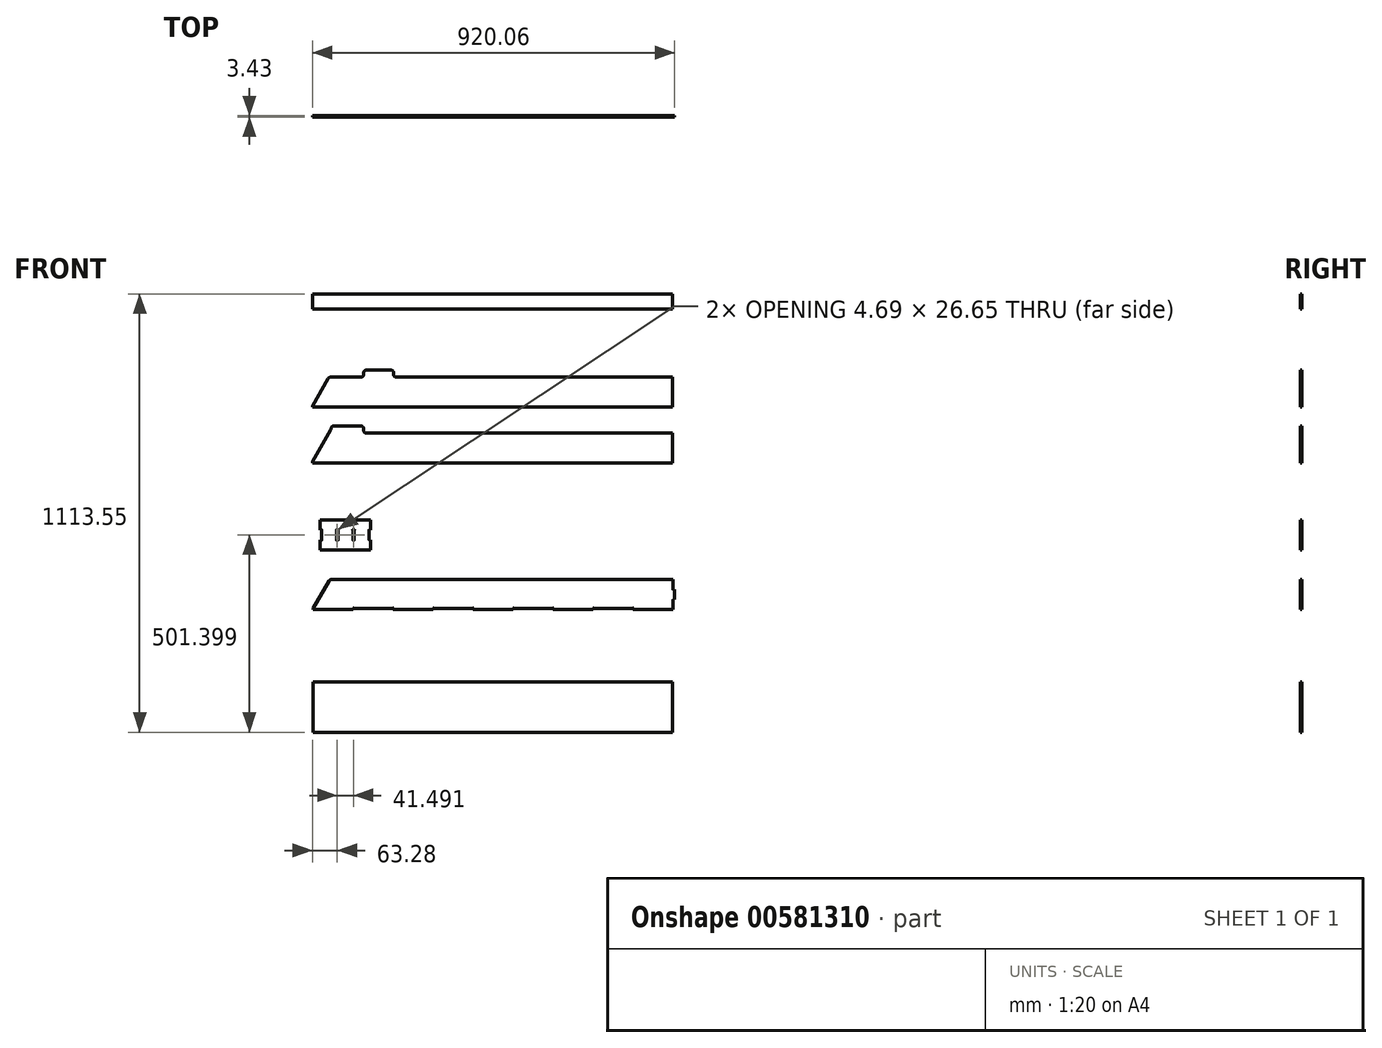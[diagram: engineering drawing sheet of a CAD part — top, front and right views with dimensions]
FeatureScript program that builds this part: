
annotation { "Feature Type Name" : "Feature", "Feature Type Description" : "" }
export const myFeature = defineFeature(function(context is Context, id is Id, definition is map)
    precondition{}
    {
        {
            var Q0;
            Q0=qCreatedBy(makeId("Front.planeOp"),FACE);
            var sketch = newSketch(context, id + "F0", { "sketchPlane" : qUnion([Q0])});
            skLineSegment(sketch, "E0", {"start": v(-436.83, -273.53) * mm, "end": v(477.57, -273.53) * mm, "construction": true});
            skLineSegment(sketch, "E1", {"start": v(20.37, -273.53) * mm, "end": v(20.37, -235.43) * mm, "construction": true});
            skLineSegment(sketch, "E2.trimOffspring", {"start": v(-333.7, -235.43) * mm, "end": v(-234.44, -235.43) * mm});
            skLineSegment(sketch, "E3", {"start": v(-436.83, -311.63) * mm, "end": v(-436.83, -273.53) * mm});
            skLineSegment(sketch, "E4", {"start": v(477.57, -235.43) * mm, "end": v(477.57, -260.24) * mm});
            skLineSegment(sketch, "E5", {"start": v(-438.12, -216.33) * mm, "end": v(-437.43, -216.38) * mm, "construction": true});
            skPoint(sketch, "E6.newPointA", {"position": v(-437.43, -216.33) * mm});
            skPoint(sketch, "E6.newPointB", {"position": v(-438.12, -235.43) * mm});
            skArc(sketch, "E7", {"start": v(23.28, -210.74) * mm, "mid": v(20.37, -210.03) * mm, "end": v(17.45, -210.74) * mm});
            skLineSegment(sketch, "E8", {"start": v(14.02, -216.38) * mm, "end": v(26.72, -216.38) * mm, "construction": true});
            skLineSegment(sketch, "E9", {"start": v(14.02, -216.33) * mm, "end": v(14.02, -216.38) * mm});
            skLineSegment(sketch, "E10.trimOffspring", {"start": v(72.7, -235.43) * mm, "end": v(171.96, -235.43) * mm});
            skPoint(sketch, "E11.visualSharp", {"position": v(14.02, -235.43) * mm});
            skPoint(sketch, "E12.visualSharp", {"position": v(34.05, -235.43) * mm});
            skArc(sketch, "E13.MirrorCS", {"start": v(24.77, -335.26) * mm, "mid": v(20.37, -337.03) * mm, "end": v(15.96, -335.26) * mm});
            skCircle(sketch, "E14.MirrorC", {"center": v(20.37, -330.68) * mm, "radius": 2.67 * mm});
            skLineSegment(sketch, "E15.trimOffspring", {"start": v(-436.83, -273.53) * mm, "end": v(-436.83, -239.3) * mm});
            skLineSegment(sketch, "E16.MirrorCS", {"start": v(480.98, -260.75) * mm, "end": v(480.98, -273.5) * mm});
            skLineSegment(sketch, "E17.MirrorCS", {"start": v(478.04, -286.15) * mm, "end": v(479.7, -286.15) * mm});
            skLineSegment(sketch, "E18", {"start": v(480.98, -260.75) * mm, "end": v(478.07, -260.75) * mm});
            skLineSegment(sketch, "E19.trimOffspring", {"start": v(477.57, -286.82) * mm, "end": v(477.57, -311.63) * mm});
            skArc(sketch, "E20", {"start": v(477.57, -260.24) * mm, "mid": v(477.2, -261.1) * mm, "end": v(478.07, -260.75) * mm});
            skArc(sketch, "E21.MirrorC", {"start": v(477.57, -286.82) * mm, "mid": v(477.15, -286.02) * mm, "end": v(478.04, -286.15) * mm});
            skLineSegment(sketch, "E22.MirrorCS", {"start": v(480.98, -286.32) * mm, "end": v(480.98, -273.57) * mm});
            skPoint(sketch, "E23.MirrorCS.start.orphan", {"position": v(477.57, -273.53) * mm});
            skPoint(sketch, "E12.filletArc.start.orphan", {"position": v(34.05, -229.12) * mm});
            skPoint(sketch, "E24.orphan", {"position": v(40.4, -235.43) * mm});
            skLineSegment(sketch, "E25", {"start": v(-335.23, -315.05) * mm, "end": v(-335.23, -312.14) * mm});
            skLineSegment(sketch, "E26", {"start": v(-334.73, -311.63) * mm, "end": v(-234.14, -311.63) * mm});
            skLineSegment(sketch, "E27", {"start": v(-233.63, -311.24) * mm, "end": v(-233.63, -312.14) * mm});
            skLineSegment(sketch, "E28", {"start": v(-132.03, -312.14) * mm, "end": v(-132.03, -311.24) * mm});
            skLineSegment(sketch, "E29", {"start": v(-131.53, -311.63) * mm, "end": v(-30.94, -311.63) * mm});
            skLineSegment(sketch, "E30", {"start": v(-30.43, -290.61) * mm, "end": v(-30.43, -312.14) * mm});
            skLineSegment(sketch, "E31", {"start": v(-182.83, -311.24) * mm, "end": v(-182.83, -379.42) * mm, "construction": true});
            skPoint(sketch, "E31.endSnap0", {"position": v(-182.83, -311.24) * mm});
            skCircle(sketch, "E32", {"center": v(-182.83, -330.53) * mm, "radius": 2.67 * mm});
            skArc(sketch, "E33", {"start": v(-185.77, -336.16) * mm, "mid": v(-184.34, -336.7) * mm, "end": v(-182.83, -336.88) * mm});
            skLineSegment(sketch, "E34", {"start": v(-233.63, -311.24) * mm, "end": v(-185.77, -336.16) * mm});
            skArc(sketch, "E35", {"start": v(-234.14, -311.63) * mm, "mid": v(-233.28, -311.27) * mm, "end": v(-233.63, -312.14) * mm});
            skArc(sketch, "E36.MirrorCS", {"start": v(-179.9, -336.16) * mm, "mid": v(-181.33, -336.7) * mm, "end": v(-182.83, -336.88) * mm});
            skLineSegment(sketch, "E37.MirrorCS", {"start": v(-132.03, -311.24) * mm, "end": v(-179.9, -336.16) * mm});
            skArc(sketch, "E38.MirrorCS", {"start": v(-131.53, -311.63) * mm, "mid": v(-132.4, -311.27) * mm, "end": v(-132.03, -312.14) * mm});
            skArc(sketch, "E39", {"start": v(-335.23, -312.14) * mm, "mid": v(-335.6, -311.27) * mm, "end": v(-334.73, -311.63) * mm});
            skLineSegment(sketch, "E40", {"start": v(-30.43, -290.61) * mm, "end": v(15.96, -335.26) * mm});
            skPoint(sketch, "E41.orphan", {"position": v(-403.8, -235.43) * mm});
            skLineSegment(sketch, "E42.MirrorCS", {"start": v(71.17, -290.61) * mm, "end": v(24.77, -335.26) * mm});
            skLineSegment(sketch, "E43.MirrorCS", {"start": v(71.17, -290.61) * mm, "end": v(71.17, -312.14) * mm});
            skLineSegment(sketch, "E44.MirrorCS", {"start": v(172.26, -311.63) * mm, "end": v(71.67, -311.63) * mm});
            skLineSegment(sketch, "E45.MirrorCS", {"start": v(172.77, -312.14) * mm, "end": v(172.77, -311.24) * mm});
            skArc(sketch, "E46.MirrorCS", {"start": v(172.26, -311.63) * mm, "mid": v(173.12, -311.27) * mm, "end": v(172.77, -312.14) * mm});
            skLineSegment(sketch, "E47.MirrorCS", {"start": v(172.77, -311.24) * mm, "end": v(220.63, -336.16) * mm});
            skArc(sketch, "E48.MirrorCS", {"start": v(220.63, -336.16) * mm, "mid": v(222.06, -336.7) * mm, "end": v(223.57, -336.88) * mm});
            skCircle(sketch, "E49.MirrorC", {"center": v(223.57, -330.53) * mm, "radius": 2.67 * mm});
            skArc(sketch, "E50.MirrorCS", {"start": v(226.5, -336.16) * mm, "mid": v(225.07, -336.7) * mm, "end": v(223.57, -336.88) * mm});
            skLineSegment(sketch, "E51.MirrorCS", {"start": v(274.37, -311.24) * mm, "end": v(226.5, -336.16) * mm});
            skLineSegment(sketch, "E52.MirrorCS", {"start": v(274.37, -311.24) * mm, "end": v(274.37, -312.14) * mm});
            skArc(sketch, "E53.MirrorCS", {"start": v(274.87, -311.63) * mm, "mid": v(274, -311.27) * mm, "end": v(274.37, -312.14) * mm});
            skLineSegment(sketch, "E54.MirrorCS", {"start": v(375.46, -311.63) * mm, "end": v(274.87, -311.63) * mm});
            skArc(sketch, "E55.MirrorCS", {"start": v(375.97, -312.14) * mm, "mid": v(376.32, -311.27) * mm, "end": v(375.46, -311.63) * mm});
            skLineSegment(sketch, "E56.MirrorCS", {"start": v(375.97, -315.05) * mm, "end": v(375.97, -312.14) * mm});
            skArc(sketch, "E57", {"start": v(71.17, -312.14) * mm, "mid": v(70.8, -311.27) * mm, "end": v(71.67, -311.63) * mm});
            skArc(sketch, "E58", {"start": v(-30.94, -311.63) * mm, "mid": v(-30.08, -311.27) * mm, "end": v(-30.43, -312.14) * mm});
            skCircle(sketch, "E59", {"center": v(-386.03, -216.38) * mm, "radius": 2.67 * mm});
            skArc(sketch, "E60", {"start": v(-388.95, -210.74) * mm, "mid": v(-386.03, -210.03) * mm, "end": v(-383.12, -210.74) * mm});
            skLineSegment(sketch, "E61", {"start": v(-433.4, -233.66) * mm, "end": v(-388.95, -210.74) * mm});
            skLineSegment(sketch, "E62", {"start": v(-386.03, -216.38) * mm, "end": v(-386.03, -233.2) * mm, "construction": true});
            skPoint(sketch, "E63.orphan", {"position": v(-392.38, -216.38) * mm});
            skPoint(sketch, "E64.visualSharp", {"position": v(-436.83, -235.43) * mm});
            skArc(sketch, "E64.filletArc", {"start": v(-433.4, -233.66) * mm, "mid": v(-435.9, -236) * mm, "end": v(-436.83, -239.3) * mm});
            skLineSegment(sketch, "E65.MirrorCS", {"start": v(-336.6, -234.72) * mm, "end": v(-383.12, -210.74) * mm});
            skPoint(sketch, "E66.orphan", {"position": v(-379.68, -216.38) * mm});
            skArc(sketch, "E67.filletArc", {"start": v(-336.6, -234.72) * mm, "mid": v(-335.2, -235.25) * mm, "end": v(-333.7, -235.43) * mm});
            skLineSegment(sketch, "E68.MirrorCS", {"start": v(-436.83, -311.63) * mm, "end": v(-388.95, -336.32) * mm});
            skArc(sketch, "E69.MirrorCS", {"start": v(-388.95, -336.32) * mm, "mid": v(-386.03, -337.03) * mm, "end": v(-383.12, -336.32) * mm});
            skCircle(sketch, "E70.MirrorC", {"center": v(-386.03, -330.68) * mm, "radius": 2.67 * mm});
            skLineSegment(sketch, "E71.MirrorCS", {"start": v(-335.23, -311.63) * mm, "end": v(-383.12, -336.32) * mm});
            skPoint(sketch, "E72.orphan", {"position": v(-436.83, -311.63) * mm});
            skLineSegment(sketch, "E73.MirrorCS", {"start": v(69.8, -234.72) * mm, "end": v(23.28, -210.74) * mm});
            skCircle(sketch, "E74.MirrorC", {"center": v(20.37, -216.38) * mm, "radius": 2.67 * mm});
            skLineSegment(sketch, "E75.MirrorCS", {"start": v(-29.07, -234.72) * mm, "end": v(17.45, -210.74) * mm});
            skArc(sketch, "E76.MirrorCS", {"start": v(-29.07, -234.72) * mm, "mid": v(-30.48, -235.25) * mm, "end": v(-31.98, -235.43) * mm});
            skPoint(sketch, "E77.orphan", {"position": v(-3.75, -235.43) * mm});
            skPoint(sketch, "E78.orphan", {"position": v(44.48, -235.43) * mm});
            skPoint(sketch, "E79.visualSharp", {"position": v(71.17, -235.43) * mm});
            skArc(sketch, "E79.filletArc", {"start": v(69.8, -234.72) * mm, "mid": v(71.2, -235.25) * mm, "end": v(72.7, -235.43) * mm});
            skLineSegment(sketch, "E80.MirrorCS", {"start": v(375.97, -311.63) * mm, "end": v(423.85, -336.32) * mm});
            skArc(sketch, "E81.MirrorCS", {"start": v(429.68, -336.32) * mm, "mid": v(426.77, -337.03) * mm, "end": v(423.85, -336.32) * mm});
            skLineSegment(sketch, "E82.MirrorCS", {"start": v(477.57, -311.63) * mm, "end": v(429.68, -336.32) * mm});
            skCircle(sketch, "E83.MirrorC", {"center": v(426.77, -330.68) * mm, "radius": 2.67 * mm});
            skLineSegment(sketch, "E84.MirrorCS", {"start": v(477.57, -235.43) * mm, "end": v(429.68, -210.74) * mm});
            skArc(sketch, "E85.MirrorCS", {"start": v(429.68, -210.74) * mm, "mid": v(426.77, -210.03) * mm, "end": v(423.85, -210.74) * mm});
            skCircle(sketch, "E86.MirrorC", {"center": v(426.77, -216.38) * mm, "radius": 2.67 * mm});
            skLineSegment(sketch, "E87.MirrorCS", {"start": v(377.33, -234.72) * mm, "end": v(423.85, -210.74) * mm});
            skPoint(sketch, "E88.orphan", {"position": v(444.53, -235.43) * mm});
            skPoint(sketch, "E89.visualSharp", {"position": v(375.97, -235.43) * mm});
            skArc(sketch, "E89.filletArc", {"start": v(374.42, -235.43) * mm, "mid": v(375.92, -235.25) * mm, "end": v(377.33, -234.72) * mm});
            skLineSegment(sketch, "E90.MirrorCS", {"start": v(-231.5, -234.71) * mm, "end": v(-185.77, -210.9) * mm});
            skLineSegment(sketch, "E91.MirrorCS", {"start": v(-134.16, -234.71) * mm, "end": v(-179.9, -210.9) * mm});
            skArc(sketch, "E92.MirrorCS", {"start": v(-185.77, -210.9) * mm, "mid": v(-184.34, -210.36) * mm, "end": v(-182.83, -210.18) * mm});
            skArc(sketch, "E93.MirrorCS", {"start": v(-179.9, -210.9) * mm, "mid": v(-181.33, -210.36) * mm, "end": v(-182.83, -210.18) * mm});
            skCircle(sketch, "E94.MirrorC", {"center": v(-182.83, -216.53) * mm, "radius": 2.67 * mm});
            skLineSegment(sketch, "E95.MirrorCS", {"start": v(174.9, -234.71) * mm, "end": v(220.63, -210.9) * mm});
            skArc(sketch, "E96.MirrorCS", {"start": v(220.63, -210.9) * mm, "mid": v(222.06, -210.36) * mm, "end": v(223.57, -210.18) * mm});
            skArc(sketch, "E97.MirrorCS", {"start": v(226.5, -210.9) * mm, "mid": v(225.07, -210.36) * mm, "end": v(223.57, -210.18) * mm});
            skLineSegment(sketch, "E98.MirrorCS", {"start": v(272.24, -234.71) * mm, "end": v(226.5, -210.9) * mm});
            skCircle(sketch, "E99.MirrorC", {"center": v(223.57, -216.53) * mm, "radius": 2.67 * mm});
            skLineSegment(sketch, "E100.trimOffspring", {"start": v(-131.23, -235.43) * mm, "end": v(-31.98, -235.43) * mm});
            skPoint(sketch, "E101.newPointA", {"position": v(-233.63, -235.82) * mm});
            skArc(sketch, "E101.filletArc", {"start": v(-234.44, -235.43) * mm, "mid": v(-232.93, -235.25) * mm, "end": v(-231.5, -234.71) * mm});
            skPoint(sketch, "E102.newPointA", {"position": v(-132.03, -235.82) * mm});
            skArc(sketch, "E102.filletArc", {"start": v(-134.16, -234.71) * mm, "mid": v(-132.74, -235.25) * mm, "end": v(-131.23, -235.43) * mm});
            skLineSegment(sketch, "E103.trimOffspring", {"start": v(275.17, -235.43) * mm, "end": v(374.42, -235.43) * mm});
            skPoint(sketch, "E104.newPointA", {"position": v(172.77, -235.82) * mm});
            skArc(sketch, "E104.filletArc", {"start": v(171.96, -235.43) * mm, "mid": v(173.47, -235.25) * mm, "end": v(174.9, -234.71) * mm});
            skPoint(sketch, "E105.newPointA", {"position": v(274.37, -235.82) * mm});
            skArc(sketch, "E105.filletArc", {"start": v(272.24, -234.71) * mm, "mid": v(273.66, -235.25) * mm, "end": v(275.17, -235.43) * mm});
            skSolve(sketch);
        }
        {
            var Q0;
            Q0=qCreatedBy(makeId("Front.planeOp"),FACE);
            var sketch = newSketch(context, id + "F1", { "sketchPlane" : qUnion([Q0])});
            skLineSegment(sketch, "E106.0", {"start": v(-444.44, -324.66) * mm, "end": v(-444.44, -235.76) * mm});
            skLineSegment(sketch, "E107.0", {"start": v(469.96, -235.76) * mm, "end": v(469.96, -324.66) * mm});
            skLineSegment(sketch, "E108.bottom", {"start": v(-444.44, -143.46) * mm, "end": v(469.96, -143.46) * mm});
            skLineSegment(sketch, "E108.top", {"start": v(-444.44, -181.56) * mm, "end": v(469.96, -181.56) * mm});
            skLineSegment(sketch, "E108.left", {"start": v(-444.44, -143.46) * mm, "end": v(-444.44, -181.56) * mm});
            skLineSegment(sketch, "E108.right", {"start": v(469.96, -143.46) * mm, "end": v(469.96, -181.56) * mm});
            skSolve(sketch);
        }
        {
            var Q0;
            Q0=makeQuery(id+"F1.imprint","IMPRINT",FACE,{"disambiguationData":[TD([[makeQuery(id+"F1.imprint","IMPRINT",EDGE,{"derivedFrom":sQuery(id+"F1.wireOp",EDGE,"E108.bottom")}),-1.0]])]});
            extrude(context, id + "F2", {"entities" : qUnion([Q0]), "depth" : 3.42 * mm, "offsetDistance" : 25.4 * mm});
        }
        {
            var Q0;
            Q0=qCreatedBy(makeId("Front.planeOp"),FACE);
            var sketch = newSketch(context, id + "F3", { "sketchPlane" : qUnion([Q0])});
            skLineSegment(sketch, "E109.0", {"start": v(-444.44, -324.66) * mm, "end": v(-444.44, -235.76) * mm});
            skLineSegment(sketch, "E110.0", {"start": v(469.96, -235.76) * mm, "end": v(469.96, -324.66) * mm});
            skLineSegment(sketch, "E111.bottom", {"start": v(-398.75, -354.83) * mm, "end": v(-320.6, -354.83) * mm});
            skLineSegment(sketch, "E111.top", {"start": v(-444.44, -431.03) * mm, "end": v(469.96, -431.03) * mm});
            skLineSegment(sketch, "E111.right", {"start": v(469.96, -354.83) * mm, "end": v(469.96, -431.03) * mm});
            skLineSegment(sketch, "E112.top", {"start": v(-307.9, -337.05) * mm, "end": v(-244.4, -337.05) * mm});
            skLineSegment(sketch, "E112.left", {"start": v(-314.24, -348.48) * mm, "end": v(-314.24, -343.4) * mm});
            skLineSegment(sketch, "E112.right", {"start": v(-238.04, -348.48) * mm, "end": v(-238.04, -343.4) * mm});
            skLineSegment(sketch, "E113.trimOffspring", {"start": v(-231.7, -354.83) * mm, "end": v(469.96, -354.83) * mm});
            skPoint(sketch, "E114.visualSharp", {"position": v(-314.24, -337.05) * mm});
            skArc(sketch, "E114.filletArc", {"start": v(-307.9, -337.05) * mm, "mid": v(-312.38, -338.9) * mm, "end": v(-314.24, -343.4) * mm});
            skPoint(sketch, "E115.visualSharp", {"position": v(-238.04, -337.05) * mm});
            skArc(sketch, "E115.filletArc", {"start": v(-238.04, -343.4) * mm, "mid": v(-239.9, -338.9) * mm, "end": v(-244.4, -337.05) * mm});
            skPoint(sketch, "E116.visualSharp", {"position": v(-314.24, -354.83) * mm});
            skArc(sketch, "E116.filletArc", {"start": v(-320.6, -354.83) * mm, "mid": v(-316.1, -352.97) * mm, "end": v(-314.24, -348.48) * mm});
            skPoint(sketch, "E117.visualSharp", {"position": v(-238.04, -354.83) * mm});
            skArc(sketch, "E117.filletArc", {"start": v(-238.04, -348.48) * mm, "mid": v(-236.18, -352.97) * mm, "end": v(-231.7, -354.83) * mm});
            skLineSegment(sketch, "E118", {"start": v(-444.44, -427.61) * mm, "end": v(-404.25, -358) * mm});
            skPoint(sketch, "E119.visualSharp", {"position": v(-402.42, -354.83) * mm});
            skArc(sketch, "E119.filletArc", {"start": v(-398.75, -354.83) * mm, "mid": v(-401.93, -355.68) * mm, "end": v(-404.25, -358) * mm});
            skLineSegment(sketch, "E120", {"start": v(-444.44, -324.66) * mm, "end": v(-444.44, -471.8) * mm, "construction": true});
            skLineSegment(sketch, "E121", {"start": v(469.96, -324.66) * mm, "end": v(469.96, -480.39) * mm, "construction": true});
            skPoint(sketch, "E122.0", {"position": v(-355.54, -235.76) * mm});
            skLineSegment(sketch, "E123", {"start": v(-444.44, -427.61) * mm, "end": v(-444.44, -431.03) * mm});
            skSolve(sketch);
        }
        {
            var Q0;
            Q0=makeQuery(id+"F3.imprint","IMPRINT",FACE,{"disambiguationData":[TD([[makeQuery(id+"F3.imprint","IMPRINT",EDGE,{"derivedFrom":sQuery(id+"F3.wireOp",EDGE,"E111.bottom")}),-1.0]])]});
            extrude(context, id + "F4", {"entities" : qUnion([Q0]), "depth" : 3.42 * mm, "offsetDistance" : 25.4 * mm});
        }
        {
            var Q0;
            Q0=qCreatedBy(makeId("Front.planeOp"),FACE);
            var sketch = newSketch(context, id + "F5", { "sketchPlane" : qUnion([Q0])});
            skPoint(sketch, "E124.0", {"position": v(-444.44, -431.03) * mm});
            skLineSegment(sketch, "E125.0", {"start": v(469.96, -354.83) * mm, "end": v(469.96, -431.03) * mm});
            skLineSegment(sketch, "E126", {"start": v(-444.44, -431.03) * mm, "end": v(-444.44, -515.14) * mm, "construction": true});
            skLineSegment(sketch, "E127", {"start": v(469.96, -431.03) * mm, "end": v(469.96, -621.54) * mm, "construction": true});
            skLineSegment(sketch, "E128", {"start": v(469.96, -496.68) * mm, "end": v(469.96, -572.88) * mm});
            skLineSegment(sketch, "E129", {"start": v(469.96, -572.88) * mm, "end": v(-444.44, -572.88) * mm});
            skPoint(sketch, "E130.0", {"position": v(-238.04, -348.48) * mm});
            skLineSegment(sketch, "E131.bottom", {"start": v(-390.43, -478.9) * mm, "end": v(-320.58, -478.9) * mm});
            skLineSegment(sketch, "E131.left", {"start": v(-396.78, -485.21) * mm, "end": v(-396.78, -485.25) * mm});
            skLineSegment(sketch, "E131.right", {"start": v(-314.23, -485.25) * mm, "end": v(-314.23, -490.33) * mm});
            skLineSegment(sketch, "E132.trimOffspring", {"start": v(-307.88, -496.68) * mm, "end": v(469.96, -496.68) * mm});
            skPoint(sketch, "E133.visualSharp", {"position": v(-396.78, -478.9) * mm});
            skArc(sketch, "E133.filletArc", {"start": v(-390.43, -478.9) * mm, "mid": v(-394.92, -480.76) * mm, "end": v(-396.78, -485.25) * mm});
            skPoint(sketch, "E134.visualSharp", {"position": v(-314.23, -478.9) * mm});
            skArc(sketch, "E134.filletArc", {"start": v(-314.23, -485.25) * mm, "mid": v(-316.1, -480.76) * mm, "end": v(-320.58, -478.9) * mm});
            skPoint(sketch, "E135.visualSharp", {"position": v(-314.23, -496.68) * mm});
            skArc(sketch, "E135.filletArc", {"start": v(-314.23, -490.33) * mm, "mid": v(-312.37, -494.82) * mm, "end": v(-307.88, -496.68) * mm});
            skPoint(sketch, "E136.visualSharp", {"position": v(-396.78, -515.14) * mm});
            skLineSegment(sketch, "E137", {"start": v(-444.44, -569.47) * mm, "end": v(-397.63, -488.39) * mm});
            skLineSegment(sketch, "E138.trimOffspring", {"start": v(-444.44, -569.47) * mm, "end": v(-444.44, -621.54) * mm, "construction": true});
            skLineSegment(sketch, "E139", {"start": v(-307.88, -496.68) * mm, "end": v(-396.78, -496.68) * mm, "construction": true});
            skArc(sketch, "E140.filletArc", {"start": v(-397.63, -488.39) * mm, "mid": v(-397, -486.86) * mm, "end": v(-396.78, -485.21) * mm});
            skLineSegment(sketch, "E141", {"start": v(-444.44, -572.88) * mm, "end": v(-444.44, -569.47) * mm});
            skSolve(sketch);
        }
        {
            var Q0;
            Q0=makeQuery(id+"F5.imprint","IMPRINT",FACE,{"disambiguationData":[TD([[makeQuery(id+"F5.imprint","IMPRINT",EDGE,{"derivedFrom":sQuery(id+"F5.wireOp",EDGE,"E128")}),-1.0]])]});
            extrude(context, id + "F6", {"entities" : qUnion([Q0]), "depth" : 3.4 * mm, "offsetDistance" : 25.4 * mm});
        }
        {
            var Q0;
            Q0=qCreatedBy(makeId("Front.planeOp"),FACE);
            var sketch = newSketch(context, id + "F7", { "sketchPlane" : qUnion([Q0])});
            skLineSegment(sketch, "E142.bottom", {"start": v(-424.4, -717.51) * mm, "end": v(-296.43, -717.51) * mm});
            skLineSegment(sketch, "E142.top", {"start": v(-424.4, -793.71) * mm, "end": v(-296.43, -793.71) * mm});
            skLineSegment(sketch, "E142.left", {"start": v(-424.4, -717.51) * mm, "end": v(-424.4, -742.78) * mm});
            skLineSegment(sketch, "E142.right", {"start": v(-296.43, -717.51) * mm, "end": v(-296.43, -742.78) * mm});
            skLineSegment(sketch, "E143", {"start": v(-424.4, -755.61) * mm, "end": v(-296.43, -755.61) * mm, "construction": true});
            skLineSegment(sketch, "E144", {"start": v(-360.41, -717.51) * mm, "end": v(-360.41, -793.71) * mm, "construction": true});
            skLineSegment(sketch, "E145", {"start": v(-424.4, -742.78) * mm, "end": v(-421.49, -742.78) * mm});
            skLineSegment(sketch, "E146", {"start": v(-420.98, -743.3) * mm, "end": v(-420.98, -755.61) * mm});
            skLineSegment(sketch, "E147.MirrorCS", {"start": v(-420.98, -767.93) * mm, "end": v(-420.98, -755.61) * mm});
            skLineSegment(sketch, "E148.MirrorCS", {"start": v(-424.4, -768.44) * mm, "end": v(-421.49, -768.44) * mm});
            skLineSegment(sketch, "E149.MirrorCS", {"start": v(-299.85, -743.3) * mm, "end": v(-299.85, -755.61) * mm});
            skLineSegment(sketch, "E150.MirrorCS", {"start": v(-296.43, -742.78) * mm, "end": v(-299.34, -742.78) * mm});
            skLineSegment(sketch, "E151.MirrorCS", {"start": v(-299.85, -767.93) * mm, "end": v(-299.85, -755.61) * mm});
            skLineSegment(sketch, "E152.MirrorCS", {"start": v(-296.43, -768.44) * mm, "end": v(-299.34, -768.44) * mm});
            skLineSegment(sketch, "E153.trimOffspring", {"start": v(-424.4, -768.44) * mm, "end": v(-424.4, -793.71) * mm});
            skLineSegment(sketch, "E154.trimOffspring", {"start": v(-296.43, -768.44) * mm, "end": v(-296.43, -793.71) * mm});
            skArc(sketch, "E155", {"start": v(-420.98, -743.3) * mm, "mid": v(-420.62, -742.42) * mm, "end": v(-421.49, -742.78) * mm});
            skArc(sketch, "E156.MirrorCS", {"start": v(-420.98, -767.93) * mm, "mid": v(-420.62, -768.8) * mm, "end": v(-421.49, -768.44) * mm});
            skArc(sketch, "E157.MirrorCS", {"start": v(-299.85, -743.3) * mm, "mid": v(-300.2, -742.42) * mm, "end": v(-299.34, -742.78) * mm});
            skArc(sketch, "E158.MirrorCS", {"start": v(-299.85, -767.93) * mm, "mid": v(-300.2, -768.8) * mm, "end": v(-299.34, -768.44) * mm});
            skLineSegment(sketch, "E159", {"start": v(-421.49, -742.78) * mm, "end": v(-383, -742.78) * mm, "construction": true});
            skLineSegment(sketch, "E160.MirrorCS", {"start": v(-421.49, -768.44) * mm, "end": v(-383, -768.44) * mm, "construction": true});
            skLineSegment(sketch, "E161", {"start": v(-383, -743.3) * mm, "end": v(-383, -755.61) * mm});
            skLineSegment(sketch, "E162", {"start": v(-379.31, -743.3) * mm, "end": v(-379.31, -755.61) * mm});
            skLineSegment(sketch, "E163", {"start": v(-382.5, -742.78) * mm, "end": v(-379.82, -742.78) * mm});
            skArc(sketch, "E164", {"start": v(-382.5, -742.78) * mm, "mid": v(-383.37, -742.42) * mm, "end": v(-383, -743.3) * mm});
            skArc(sketch, "E165", {"start": v(-379.31, -743.3) * mm, "mid": v(-378.95, -742.42) * mm, "end": v(-379.82, -742.78) * mm});
            skLineSegment(sketch, "E166.trimOffspring", {"start": v(-382.5, -742.78) * mm, "end": v(-338.33, -742.78) * mm, "construction": true});
            skLineSegment(sketch, "E167.MirrorCS", {"start": v(-379.31, -767.93) * mm, "end": v(-379.31, -755.61) * mm});
            skLineSegment(sketch, "E168.MirrorCS", {"start": v(-383, -767.93) * mm, "end": v(-383, -755.61) * mm});
            skArc(sketch, "E169.MirrorCS", {"start": v(-382.5, -768.44) * mm, "mid": v(-383.37, -768.8) * mm, "end": v(-383, -767.93) * mm});
            skArc(sketch, "E170.MirrorCS", {"start": v(-379.31, -767.93) * mm, "mid": v(-378.95, -768.8) * mm, "end": v(-379.82, -768.44) * mm});
            skLineSegment(sketch, "E171.MirrorCS", {"start": v(-383, -768.44) * mm, "end": v(-379.82, -768.44) * mm});
            skLineSegment(sketch, "E172.MirrorCS", {"start": v(-341.52, -743.3) * mm, "end": v(-341.52, -755.61) * mm});
            skArc(sketch, "E173.MirrorCS", {"start": v(-341.52, -743.3) * mm, "mid": v(-341.88, -742.42) * mm, "end": v(-341, -742.78) * mm});
            skLineSegment(sketch, "E174.MirrorCS", {"start": v(-338.33, -742.78) * mm, "end": v(-341, -742.78) * mm});
            skArc(sketch, "E175.MirrorCS", {"start": v(-338.33, -742.78) * mm, "mid": v(-337.46, -742.42) * mm, "end": v(-337.82, -743.3) * mm});
            skLineSegment(sketch, "E176.MirrorCS", {"start": v(-337.82, -743.3) * mm, "end": v(-337.82, -755.61) * mm});
            skLineSegment(sketch, "E177.MirrorCS", {"start": v(-337.82, -767.93) * mm, "end": v(-337.82, -755.61) * mm});
            skLineSegment(sketch, "E178.MirrorCS", {"start": v(-341.52, -767.93) * mm, "end": v(-341.52, -755.61) * mm});
            skArc(sketch, "E179.MirrorCS", {"start": v(-341.52, -767.93) * mm, "mid": v(-341.88, -768.8) * mm, "end": v(-341, -768.44) * mm});
            skArc(sketch, "E180.MirrorCS", {"start": v(-338.33, -768.44) * mm, "mid": v(-337.46, -768.8) * mm, "end": v(-337.82, -767.93) * mm});
            skLineSegment(sketch, "E181.MirrorCS", {"start": v(-338.33, -768.44) * mm, "end": v(-341, -768.44) * mm});
            skLineSegment(sketch, "E182.trimOffspring", {"start": v(-382.5, -768.44) * mm, "end": v(-338.33, -768.44) * mm, "construction": true});
            skLineSegment(sketch, "E183.trimOffspring", {"start": v(-337.82, -768.44) * mm, "end": v(-299.34, -768.44) * mm, "construction": true});
            skLineSegment(sketch, "E184.trimOffspring", {"start": v(-337.82, -742.78) * mm, "end": v(-299.34, -742.78) * mm, "construction": true});
            skLineSegment(sketch, "E185", {"start": v(-382.88, -742.78) * mm, "end": v(-382.88, -768.44) * mm, "construction": true});
            skSolve(sketch);
        }
        {
            var Q0;
            Q0=makeQuery(id+"F7.imprint","IMPRINT",FACE,{"disambiguationData":[TD([[makeQuery(id+"F7.imprint","IMPRINT",EDGE,{"derivedFrom":sQuery(id+"F7.wireOp",EDGE,"E142.bottom")}),-1.0]])]});
            extrude(context, id + "F8", {"entities" : qUnion([Q0]), "depth" : 3.42 * mm, "offsetDistance" : 25.4 * mm});
        }
        {
            var Q0;
            Q0=qCreatedBy(makeId("Front.planeOp"),FACE);
            var sketch = newSketch(context, id + "F9", { "sketchPlane" : qUnion([Q0])});
            skPoint(sketch, "E186.0", {"position": v(-444.44, -572.88) * mm});
            skPoint(sketch, "E187.0", {"position": v(469.96, -572.88) * mm});
            skLineSegment(sketch, "E188", {"start": v(-442.2, -945.5) * mm, "end": v(-340.6, -945.5) * mm});
            skLineSegment(sketch, "E189", {"start": v(472.2, -945.5) * mm, "end": v(472.2, -920.61) * mm});
            skLineSegment(sketch, "E190", {"start": v(472.2, -869.3) * mm, "end": v(-396.5, -869.3) * mm});
            skLineSegment(sketch, "E191", {"start": v(-402, -872.48) * mm, "end": v(-442.2, -942.09) * mm});
            skLineSegment(sketch, "E192", {"start": v(-442.2, -942.09) * mm, "end": v(-442.2, -945.5) * mm});
            skPoint(sketch, "E193.visualSharp", {"position": v(-400.18, -869.3) * mm});
            skArc(sketch, "E193.filletArc", {"start": v(-396.5, -869.3) * mm, "mid": v(-399.68, -870.15) * mm, "end": v(-402, -872.48) * mm});
            skLineSegment(sketch, "E194", {"start": v(472.2, -280.2) * mm, "end": v(472.2, -894.2) * mm, "construction": true});
            skLineSegment(sketch, "E195", {"start": v(-442.2, -280.2) * mm, "end": v(-442.2, -968.57) * mm, "construction": true});
            skLineSegment(sketch, "E196.0", {"start": v(-442.2, -318) * mm, "end": v(-442.2, -229.1) * mm});
            skLineSegment(sketch, "E197.0", {"start": v(472.2, -229.1) * mm, "end": v(472.2, -260.34) * mm});
            skLineSegment(sketch, "E198", {"start": v(472.2, -907.4) * mm, "end": v(-422.17, -907.4) * mm, "construction": true});
            skLineSegment(sketch, "E199", {"start": v(472.71, -894.7) * mm, "end": v(475.62, -894.7) * mm});
            skLineSegment(sketch, "E200", {"start": v(475.62, -894.7) * mm, "end": v(475.62, -907.4) * mm});
            skArc(sketch, "E201", {"start": v(472.2, -894.2) * mm, "mid": v(471.84, -895.06) * mm, "end": v(472.71, -894.7) * mm});
            skLineSegment(sketch, "E202.trimOffspring", {"start": v(472.2, -894.2) * mm, "end": v(472.2, -869.3) * mm});
            skArc(sketch, "E203.MirrorCS", {"start": v(472.2, -920.61) * mm, "mid": v(471.84, -919.74) * mm, "end": v(472.71, -920.1) * mm});
            skLineSegment(sketch, "E204.MirrorCS", {"start": v(472.71, -920.1) * mm, "end": v(475.62, -920.1) * mm});
            skLineSegment(sketch, "E205.MirrorCS", {"start": v(475.62, -920.1) * mm, "end": v(475.62, -907.4) * mm});
            skLineSegment(sketch, "E206", {"start": v(15, -869.3) * mm, "end": v(15, -945.5) * mm, "construction": true});
            skPoint(sketch, "E206.startSnap0", {"position": v(15, -945.5) * mm});
            skLineSegment(sketch, "E207", {"start": v(-340.6, -945.5) * mm, "end": v(-340.6, -942.6) * mm});
            skLineSegment(sketch, "E208", {"start": v(-340.09, -942.09) * mm, "end": v(-239.5, -942.09) * mm});
            skLineSegment(sketch, "E209", {"start": v(-239, -942.6) * mm, "end": v(-239, -945.5) * mm});
            skLineSegment(sketch, "E210", {"start": v(-137.4, -945.5) * mm, "end": v(-137.4, -942.6) * mm});
            skLineSegment(sketch, "E211", {"start": v(-136.89, -942.09) * mm, "end": v(-36.3, -942.09) * mm});
            skLineSegment(sketch, "E212", {"start": v(-35.8, -942.6) * mm, "end": v(-35.8, -945.5) * mm});
            skLineSegment(sketch, "E213.trimOffspring", {"start": v(-239, -945.5) * mm, "end": v(-137.4, -945.5) * mm});
            skLineSegment(sketch, "E214.trimOffspring", {"start": v(-35.8, -945.5) * mm, "end": v(65.8, -945.5) * mm});
            skArc(sketch, "E215", {"start": v(-340.6, -942.6) * mm, "mid": v(-340.96, -941.73) * mm, "end": v(-340.09, -942.09) * mm});
            skArc(sketch, "E216", {"start": v(-239.5, -942.09) * mm, "mid": v(-238.64, -941.73) * mm, "end": v(-239, -942.6) * mm});
            skArc(sketch, "E217", {"start": v(-137.4, -942.6) * mm, "mid": v(-137.76, -941.73) * mm, "end": v(-136.89, -942.09) * mm});
            skArc(sketch, "E218", {"start": v(-36.3, -942.09) * mm, "mid": v(-35.44, -941.73) * mm, "end": v(-35.8, -942.6) * mm});
            skArc(sketch, "E219.MirrorCS", {"start": v(66.31, -942.09) * mm, "mid": v(65.44, -941.73) * mm, "end": v(65.8, -942.6) * mm});
            skLineSegment(sketch, "E220.MirrorCS", {"start": v(65.8, -942.6) * mm, "end": v(65.8, -945.5) * mm});
            skLineSegment(sketch, "E221.MirrorCS", {"start": v(166.9, -942.09) * mm, "end": v(66.31, -942.09) * mm});
            skArc(sketch, "E222.MirrorCS", {"start": v(167.4, -942.6) * mm, "mid": v(167.76, -941.73) * mm, "end": v(166.9, -942.09) * mm});
            skLineSegment(sketch, "E223.MirrorCS", {"start": v(167.4, -945.5) * mm, "end": v(167.4, -942.6) * mm});
            skLineSegment(sketch, "E224.MirrorCS", {"start": v(269, -942.6) * mm, "end": v(269, -945.5) * mm});
            skArc(sketch, "E225.MirrorCS", {"start": v(269.51, -942.09) * mm, "mid": v(268.64, -941.73) * mm, "end": v(269, -942.6) * mm});
            skLineSegment(sketch, "E226.MirrorCS", {"start": v(370.1, -942.09) * mm, "end": v(269.51, -942.09) * mm});
            skLineSegment(sketch, "E227.MirrorCS", {"start": v(370.6, -945.5) * mm, "end": v(370.6, -942.6) * mm});
            skArc(sketch, "E228.MirrorCS", {"start": v(370.6, -942.6) * mm, "mid": v(370.96, -941.73) * mm, "end": v(370.1, -942.09) * mm});
            skLineSegment(sketch, "E229.trimOffspring", {"start": v(167.4, -945.5) * mm, "end": v(269, -945.5) * mm});
            skLineSegment(sketch, "E230.trimOffspring", {"start": v(370.6, -945.5) * mm, "end": v(472.2, -945.5) * mm});
            skSolve(sketch);
        }
        {
            var Q0;
            Q0=makeQuery(id+"F9.imprint","IMPRINT",FACE,{"disambiguationData":[TD([[makeQuery(id+"F9.imprint","IMPRINT",EDGE,{"derivedFrom":sQuery(id+"F9.wireOp",EDGE,"E188")}),1.0]])]});
            extrude(context, id + "F10", {"entities" : qUnion([Q0]), "operationType" : NewBodyOperationType.ADD, "depth" : 3.42 * mm, "offsetDistance" : 25.4 * mm});
        }
        {
            var Q0;
            Q0=qCreatedBy(makeId("Front.planeOp"),FACE);
            var sketch = newSketch(context, id + "F11", { "sketchPlane" : qUnion([Q0])});
            skLineSegment(sketch, "E231.0", {"start": v(-442.2, -318) * mm, "end": v(-442.2, -229.1) * mm});
            skLineSegment(sketch, "E232.0", {"start": v(470.03, -286.75) * mm, "end": v(470.03, -318) * mm});
            skLineSegment(sketch, "E233", {"start": v(-442.2, -310.23) * mm, "end": v(-442.2, -1339.77) * mm, "construction": true});
            skLineSegment(sketch, "E234", {"start": v(470.03, -309.12) * mm, "end": v(470.03, -1339.77) * mm, "construction": true});
            skLineSegment(sketch, "E235", {"start": v(-442.2, -1129.05) * mm, "end": v(470.03, -1129.05) * mm});
            skLineSegment(sketch, "E236", {"start": v(-442.2, -1257.01) * mm, "end": v(470.03, -1257.01) * mm});
            skLineSegment(sketch, "E237", {"start": v(-442.2, -1129.05) * mm, "end": v(-442.2, -1257.01) * mm});
            skLineSegment(sketch, "E238", {"start": v(13.91, -1129.05) * mm, "end": v(13.91, -1257.01) * mm, "construction": true});
            skLineSegment(sketch, "E239.MirrorCS", {"start": v(470.03, -1129.05) * mm, "end": v(470.03, -1257.01) * mm});
            skSolve(sketch);
        }
        {
            var Q0;
            Q0 = qSketchRegion(id + "F11", true);
            extrude(context, id + "F12", {"entities" : qUnion([Q0]), "depth" : 3.43 * mm, "offsetDistance" : 25.4 * mm});
        }
    });
